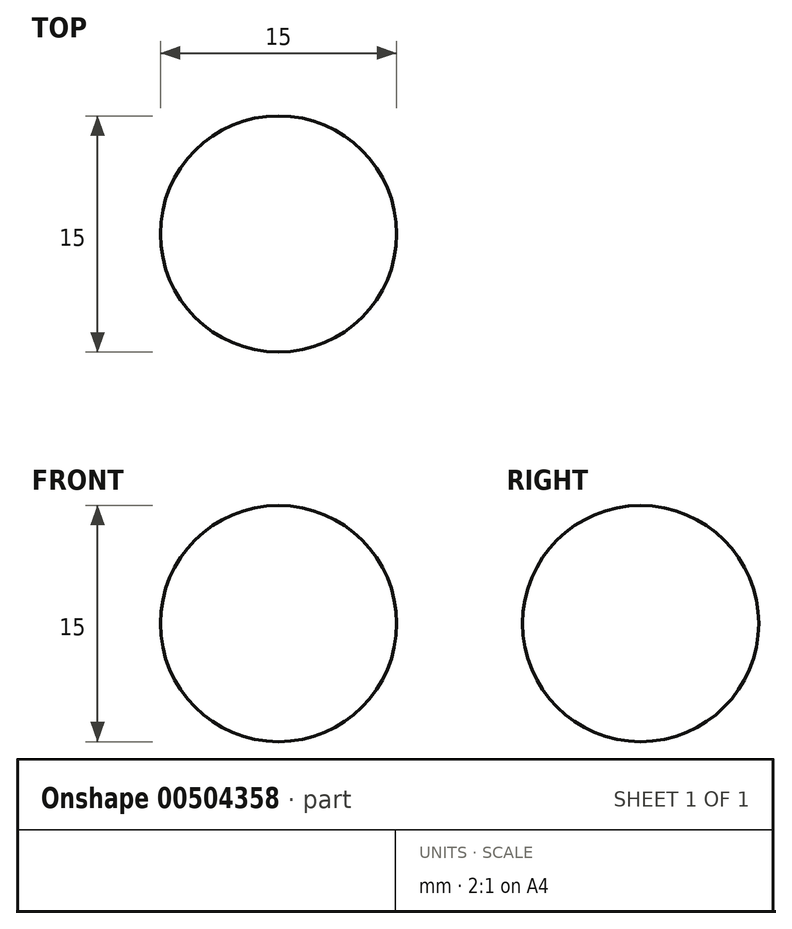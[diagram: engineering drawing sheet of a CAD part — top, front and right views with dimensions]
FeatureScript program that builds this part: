
annotation { "Feature Type Name" : "Feature", "Feature Type Description" : "" }
export const myFeature = defineFeature(function(context is Context, id is Id, definition is map)
    precondition{}
    {
        {
            var Q0;
            Q0=qCreatedBy(makeId("Front.planeOp"),FACE);
            var sketch = newSketch(context, id + "F0", { "sketchPlane" : qUnion([Q0])});
            skLineSegment(sketch, "E0", {"start": v(0, 20.61) * mm, "end": v(0, -27.65) * mm, "construction": true});
            skArc(sketch, "E1", {"start": v(0, -7.5) * mm, "mid": v(7.5, 0) * mm, "end": v(0, 7.5) * mm});
            skLineSegment(sketch, "E2", {"start": v(0, 7.5) * mm, "end": v(0, -7.5) * mm});
            skSolve(sketch);
        }
        {
            var Q0;
            Q0=makeQuery(id+"F0.imprint","IMPRINT",FACE,{"disambiguationData":[TD([[makeQuery(id+"F0.imprint","IMPRINT",EDGE,{"derivedFrom":sQuery(id+"F0.wireOp",EDGE,"E1")}),1.0]])]});
            var Q1;
            Q1=sQuery(id+"F0.wireOp",EDGE,"E0");
            revolve(context, id + "F1", {"entities" : qUnion([Q0]), "axis" : qUnion([Q1]), "revolveType" : RevolveType.FULL});
        }
    });
